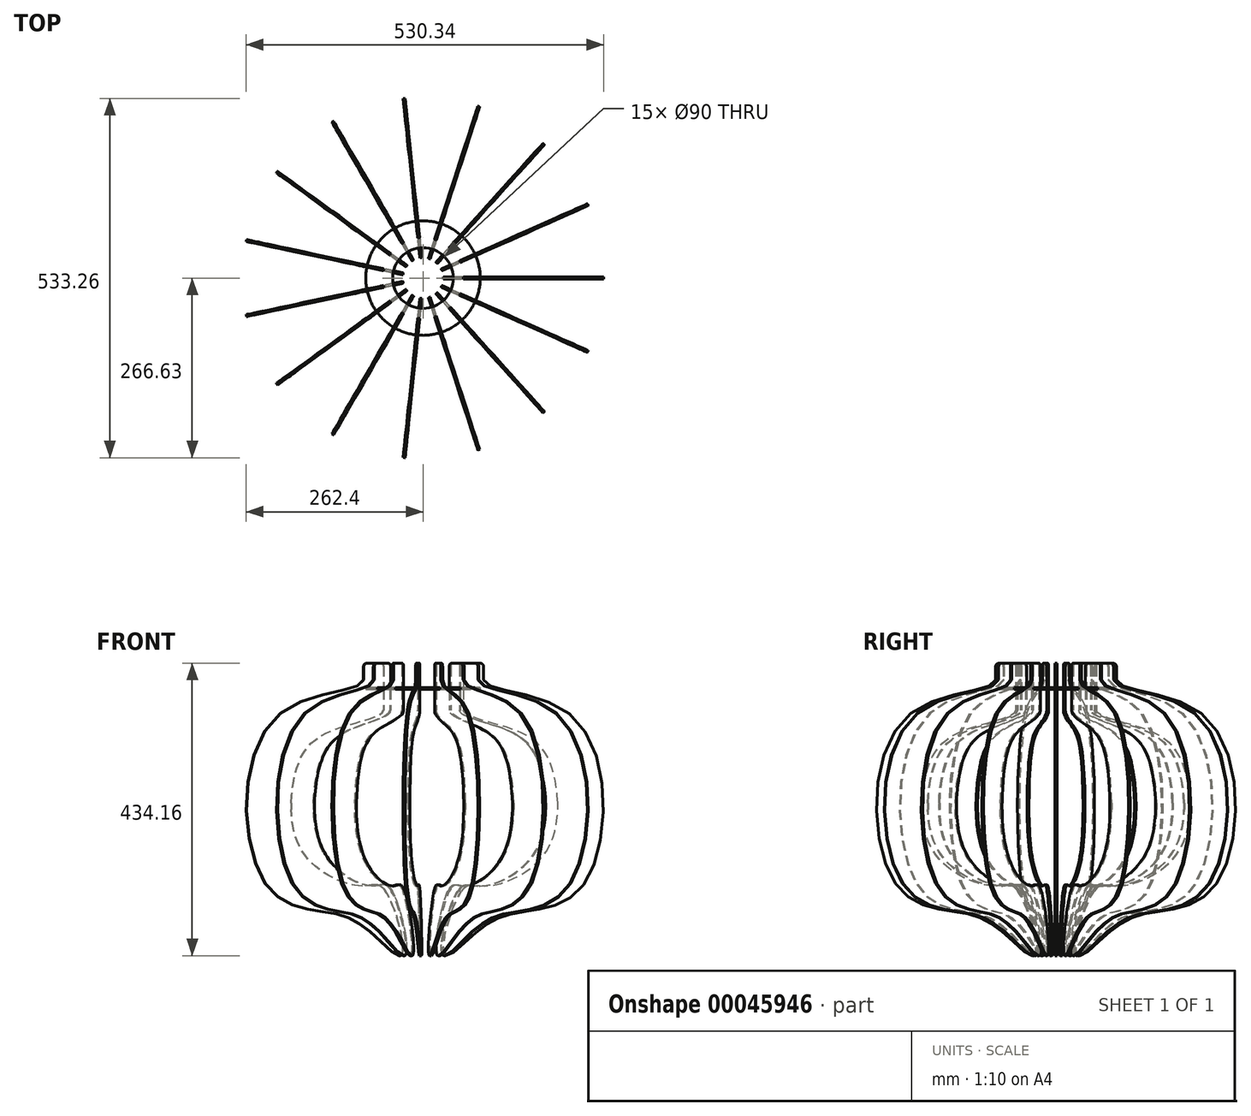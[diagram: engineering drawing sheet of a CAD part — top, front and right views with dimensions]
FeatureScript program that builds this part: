
annotation { "Feature Type Name" : "Feature", "Feature Type Description" : "" }
export const myFeature = defineFeature(function(context is Context, id is Id, definition is map)
    precondition{}
    {
        {
            var Q0;
            Q0=qCreatedBy(makeId("Front.planeOp"),FACE);
            var sketch = newSketch(context, id + "F0", { "sketchPlane" : qUnion([Q0])});
            skLineSegment(sketch, "E0", {"start": v(0, 200) * mm, "end": v(0, -200) * mm, "construction": true});
            skLineSegment(sketch, "E1", {"start": v(65, 200) * mm, "end": v(85, 200) * mm});
            skLineSegment(sketch, "E2", {"start": v(90, 195) * mm, "end": v(90, 175) * mm});
            skFitSpline(sketch, "E3", {"points": [v(90, 175) * mm, v(221.98, 120.82) * mm, v(237.52, -129.64) * mm, v(138.61, -170.79) * mm, v(76.28, -201.87) * mm, v(32.15, -232.55) * mm, v(60, -134.64) * mm, v(91.5, -130.75) * mm, v(181.6, -81.42) * mm, v(193.36, 37.63) * mm, v(143.2, 97.88) * mm, v(60, 130) * mm], "startDerivative": vector(74.1, -537.52) * mm, "endDerivative": vector(0, 383.75) * mm});
            skLineSegment(sketch, "E4", {"start": v(60, 195) * mm, "end": v(60, 130) * mm});
            skLineSegment(sketch, "E5", {"start": v(60, 130) * mm, "end": v(60, -134.64) * mm, "construction": true});
            skLineSegment(sketch, "E6", {"start": v(200, -7.46) * mm, "end": v(200, -17.46) * mm});
            skLineSegment(sketch, "E7", {"start": v(60, -134.64) * mm, "end": v(57.1, -138.27) * mm});
            skPoint(sketch, "E8.visualSharp", {"position": v(90, 200) * mm});
            skArc(sketch, "E8.filletArc", {"start": v(90, 195) * mm, "mid": v(88.54, 198.54) * mm, "end": v(85, 200) * mm});
            skPoint(sketch, "E9.visualSharp", {"position": v(60, 200) * mm});
            skArc(sketch, "E9.filletArc", {"start": v(65, 200) * mm, "mid": v(61.46, 198.54) * mm, "end": v(60, 195) * mm});
            skPoint(sketch, "E10", {"position": v(263.36, 37.63) * mm});
            skPoint(sketch, "E11", {"position": v(60, 162.5) * mm});
            skPoint(sketch, "E12", {"position": v(0, 162.5) * mm});
            skLineSegment(sketch, "E13", {"start": v(60, -134.64) * mm, "end": v(60, -232.55) * mm, "construction": true});
            skLineSegment(sketch, "E14", {"start": v(60, -232.55) * mm, "end": v(32.15, -232.55) * mm, "construction": true});
            skPoint(sketch, "E15", {"position": v(60, -168.62) * mm});
            skLineSegment(sketch, "E16", {"start": v(60, -168.62) * mm, "end": v(0, -168.62) * mm, "construction": true});
            skSolve(sketch);
        }
        {
            var Q0;
            Q0=makeQuery(id+"F0.imprint","IMPRINT",FACE,{"disambiguationData":[TD([[makeQuery(id+"F0.imprint","IMPRINT",EDGE,{"derivedFrom":sQuery(id+"F0.wireOp",EDGE,"E1")}),-1.0]])]});
            extrude(context, id + "F1", {"entities" : qUnion([Q0]), "endBound" : BoundingType.SYMMETRIC, "depth" : 3 * mm});
        }
        {
            var Q0;
            Q0=qCreatedBy(makeId("Top.planeOp"),FACE);
            cPlane(context, id + "F2", {"entities" : qUnion([Q0]), "cplaneType" : CPlaneType.OFFSET, "offset" : 161 * mm, "width" : 150 * mm, "height" : 150 * mm});
        }
        {
            var Q0;
            Q0=qCreatedBy(id+"F2.planeOp",FACE);
            var sketch = newSketch(context, id + "F3", { "sketchPlane" : qUnion([Q0])});
            skCircle(sketch, "E17", {"center": v(0, 0) * mm, "radius": 85 * mm});
            skCircle(sketch, "E18", {"center": v(0, 0) * mm, "radius": 45 * mm});
            skSolve(sketch);
        }
        {
            var Q0;
            Q0 = qSketchRegion(id + "F3", true);
            extrude(context, id + "F4", {"entities" : qUnion([Q0]), "operationType" : NewBodyOperationType.ADD, "depth" : 3 * mm});
        }
        {
            var Q0;
            Q0=makeQuery(id+"F1.opExtrude","SWEPT_BODY",BODY,{"disambiguationData":[OSD([sQuery(id+"F0.wireOp",EDGE,"E1"),sQuery(id+"F0.wireOp",EDGE,"E2"),sQuery(id+"F0.wireOp",EDGE,"E3"),sQuery(id+"F0.wireOp",EDGE,"E4"),sQuery(id+"F0.wireOp",EDGE,"E6"),sQuery(id+"F0.wireOp",EDGE,"E3"),sQuery(id+"F0.wireOp",EDGE,"E3"),sQuery(id+"F0.wireOp",EDGE,"E8.filletArc"),sQuery(id+"F0.wireOp",EDGE,"E9.filletArc")])]});
            var Q1;
            Q1=sQuery(id+"F0.wireOp",EDGE,"E0");
            circularPattern(context, id + "F5", {"entities" : qUnion([Q0]), "axis" : qUnion([Q1]), "angle" : 360 * degree, "instanceCount" : 15, "oppositeDirection" : true, "equalSpace" : true});
        }
    });
